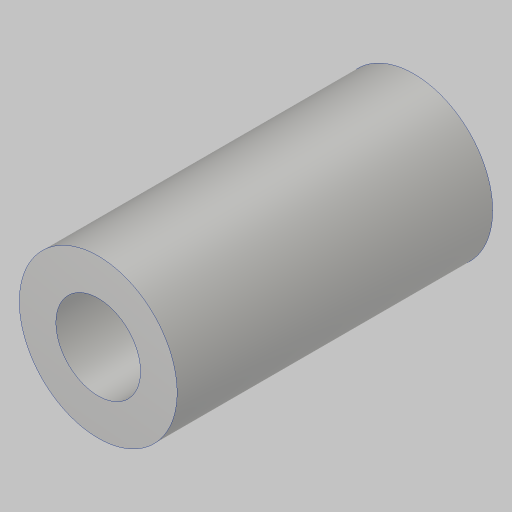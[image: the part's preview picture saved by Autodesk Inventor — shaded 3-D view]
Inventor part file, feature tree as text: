
AUTODESK INVENTOR PART (.ipt)
format: ipt  version: 2023.5 (Build 275446000, 446)  size: 171,520 bytes
history: native  units: in
note: dims shown in document units (in); Inventor stores cm internally (conversion verified against a paired STEP export)
features: extrude x1, hole x1
ambient origin geometry x8: Origin, YZ Plane, XZ Plane, XY Plane, X Axis, Y Axis, Z Axis, Center Point
bodies: Solid1 (feature_tree)
feature tree (2):
  extrude  "Extrusion1"  Depth=0.75in
  hole  "Hole1"  [1 undecoded]
note: 1 required parameter value undecoded (feature->parameter linkage not recoverable at this tier; creation-order binding heuristic only, values carry confidence <= 0.55)
